# Revit family: Accessory-Towel_Bar-KOHLER-Tone-K-27425_1
name_source: partatom
category: Specialty Equipment
units: mm (PartAtom-declared; Revit-internal decimal feet)

## family parameters
Cut with Voids When Loaded = No
Host = Face
Maintain Annotation Orientation = No
OmniClass Number = 23.31.25.25
OmniClass Title = Towel Bars
Part Type = Normal
Room Calculation Point = No
Round Connector Dimension = Use Diameter
Shared = No

## types (6) — shared parameters
ADA Compliant = No
Assembly Code = C1030200
Date Modified = 03/28/2022
Description = 18 Inch towel bar
Height = 2 9/16"
Length = 3 9/16"
Manufacturer = Kohler Co.
Master Format 2014 = 10 28 00
Master Format 2014 Name = Toilet, Bath, and Laundry Accessories
Material = Premium  Metal Construction
Product Documentation Link = https://www.us.kohler.com
Product Name = Tone
Product Page URL = http://www.us.kohler.com
URL = https://www.us.kohler.com
WaterSense Certified = No
Width = 18"

## per-type parameters (varying)
| type | Default Elevation | Finish | Model | Secondary Finish | Type |
| 2MB-Vibrant Brushed Moderne Brass | 42" | Kohler-Metal-2MB-Vibrant_Brushed_Moderne_Brass | K-27425-2MB | Kohler-Metal-2MB-Vibrant_Brushed_Moderne_Brass | 1 |
| BL-Matte Black | 42" | Kohler-Metal-BL-Matte_Black | K-27425-BL | Kohler-Metal-BL-Matte_Black | 2 |
| BMB-Matte Black With Moderne Brass | 42" | Kohler-Metal-BL-Matte_Black | K-27425-BMB | Kohler-Metal-2MB-Vibrant_Brushed_Moderne_Brass | 3 |
| BN-Vibrant Brushed Nickel | 42" | Kohler-Metal-BN-Vibrant_Brushed_Nickel | K-27425-BN | Kohler-Metal-BN-Vibrant_Brushed_Nickel | 4 |
| CBL-Polished Chrome With Matte Black | 5" | Kohler-Metal-BL-Matte_Black | K-27425-CBL | Kohler-Metal-CP-Polished_Chrome | 5 |
| CP-Polished Chrome | 42" | Kohler-Metal-CP-Polished_Chrome | K-27425-CP | Kohler-Metal-CP-Polished_Chrome | 6 |

## geometry (parser evidence)
native form markers: Sweep x5
no freeform markers — native parametric forms only
